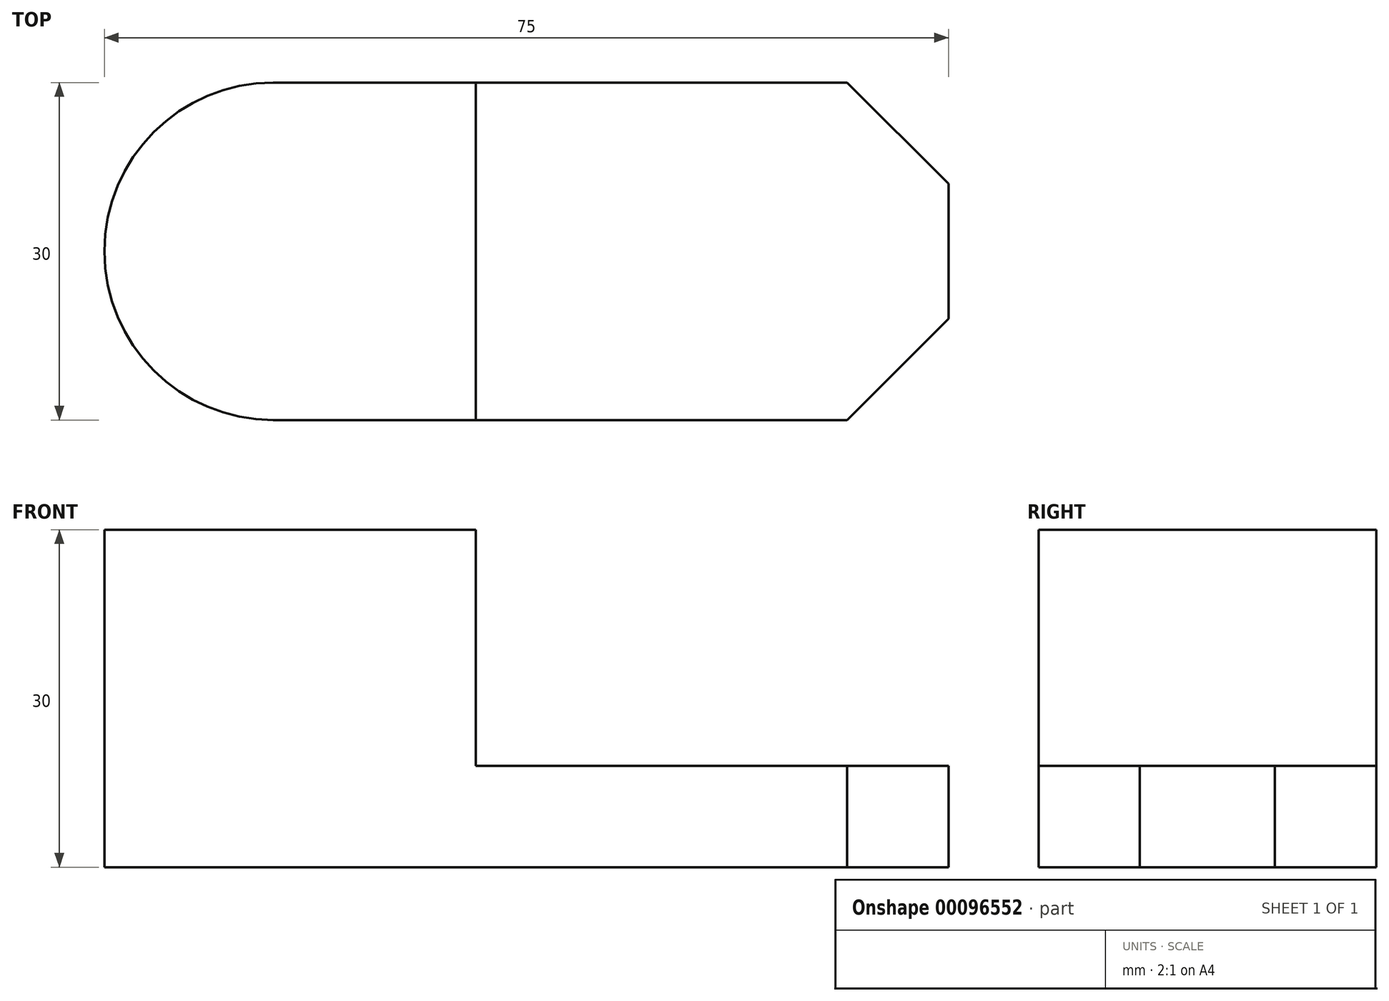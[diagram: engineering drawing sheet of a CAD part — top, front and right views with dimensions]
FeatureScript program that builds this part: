
annotation { "Feature Type Name" : "Feature", "Feature Type Description" : "" }
export const myFeature = defineFeature(function(context is Context, id is Id, definition is map)
    precondition{}
    {
        {
            var Q0;
            Q0=qCreatedBy(makeId("Top.planeOp"),FACE);
            var sketch = newSketch(context, id + "F0", { "sketchPlane" : qUnion([Q0])});
            skLineSegment(sketch, "E0.top", {"start": v(0, 30) * mm, "end": v(51, 30) * mm});
            skArc(sketch, "E1", {"start": v(0, 30) * mm, "mid": v(-15, 15) * mm, "end": v(0, 0) * mm});
            skLineSegment(sketch, "E2", {"start": v(51, 30) * mm, "end": v(60, 21) * mm});
            skLineSegment(sketch, "E3", {"start": v(60, 21) * mm, "end": v(60, 9) * mm});
            skLineSegment(sketch, "E4", {"start": v(60, 9) * mm, "end": v(51, 0) * mm});
            skLineSegment(sketch, "E5", {"start": v(0, 0) * mm, "end": v(51, 0) * mm});
            skSolve(sketch);
        }
        {
            var Q0;
            Q0=makeQuery(id+"F0.imprint","IMPRINT",FACE,{"disambiguationData":[TD([[makeQuery(id+"F0.imprint","IMPRINT",EDGE,{"derivedFrom":sQuery(id+"F0.wireOp",EDGE,"E0.top")}),-1.0]])]});
            extrude(context, id + "F1", {"entities" : qUnion([Q0]), "depth" : 9 * mm});
        }
        {
            var Q0;
            Q0=makeQuery(id+"F1.opExtrude","CAP_FACE",FACE,{"disambiguationData":[OSD([sQuery(id+"F0.wireOp",EDGE,"E0.top"),sQuery(id+"F0.wireOp",EDGE,"E1"),sQuery(id+"F0.wireOp",EDGE,"E2"),sQuery(id+"F0.wireOp",EDGE,"E3"),sQuery(id+"F0.wireOp",EDGE,"E4"),sQuery(id+"F0.wireOp",EDGE,"E5")])],"isStart":false});
            var sketch = newSketch(context, id + "F2", { "sketchPlane" : qUnion([Q0])});
            skLineSegment(sketch, "E6", {"start": v(0, 30) * mm, "end": v(18, 30) * mm});
            skLineSegment(sketch, "E7", {"start": v(18, 30) * mm, "end": v(18, 0) * mm});
            skSolve(sketch);
        }
        {
            var Q0;
            Q0=makeQuery(id+"F2.imprint","IMPRINT",FACE,{"disambiguationData":[TD([[makeQuery(id+"F2.imprint","IMPRINT",EDGE,{"derivedFrom":sQuery(id+"F2.wireOp",EDGE,"E6")}),-1.0]])]});
            var sketch = newSketch(context, id + "F3", { "sketchPlane" : qUnion([Q0])});
            skSolve(sketch);
        }
        {
            var Q0;
            Q0 = qSketchRegion(id + "F3", true);
            var Q1;
            Q1=makeQuery(id+"F2.imprint","IMPRINT",FACE,{"disambiguationData":[TD([[makeQuery(id+"F2.imprint","IMPRINT",EDGE,{"derivedFrom":sQuery(id+"F2.wireOp",EDGE,"E6")}),-1.0]])]});
            extrude(context, id + "F4", {"entities" : qUnion([Q0, Q1]), "operationType" : NewBodyOperationType.ADD, "depth" : 21 * mm});
        }
    });
